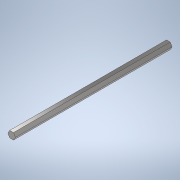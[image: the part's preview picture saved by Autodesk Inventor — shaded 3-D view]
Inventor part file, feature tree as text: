
AUTODESK INVENTOR PART (.ipt)
format: ipt  version: 2020 (Build 240168000, 168)  size: 102,400 bytes
history: native  units: in
note: dims shown in document units (in); Inventor stores cm internally (conversion verified against a paired STEP export)
features: extrude x1, sketch x1
ambient origin geometry x8: Origin, YZ Plane, XZ Plane, XY Plane, X Axis, Y Axis, Z Axis, Center Point
bodies: Solid1 (feature_tree)
feature tree (2):
  extrude  "Extrusion1"  Depth=12.0in TaperAngle=0.0deg
  sketch  "Sketch1"  dims[d0=0.5in d1=12.0in d2=0.0in]
